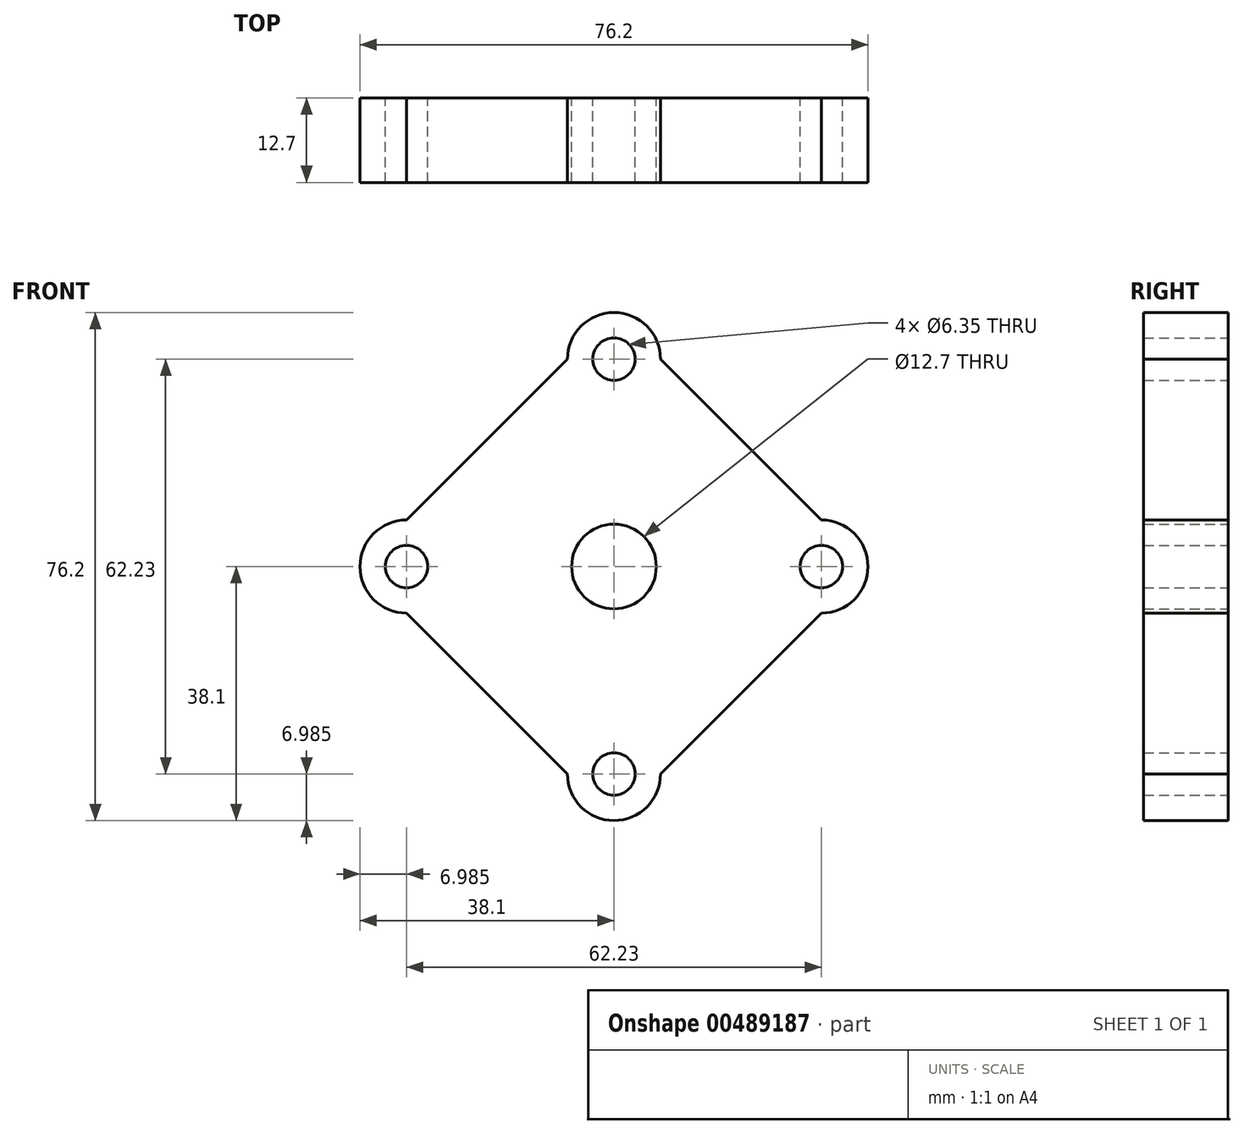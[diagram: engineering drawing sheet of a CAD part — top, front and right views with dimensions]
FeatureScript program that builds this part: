
annotation { "Feature Type Name" : "Feature", "Feature Type Description" : "" }
export const myFeature = defineFeature(function(context is Context, id is Id, definition is map)
    precondition{}
    {
        {
            var Q0;
            Q0=qCreatedBy(makeId("Front.planeOp"),FACE);
            var sketch = newSketch(context, id + "F0", { "sketchPlane" : qUnion([Q0])});
            skCircle(sketch, "E0", {"center": v(0, 0) * mm, "radius": 12.7 * mm});
            skCircle(sketch, "E1", {"center": v(0, 0) * mm, "radius": 6.35 * mm});
            skLineSegment(sketch, "E2", {"start": v(0, -12.7) * mm, "end": v(0, 38.1) * mm, "construction": true});
            skLineSegment(sketch, "E3", {"start": v(12.7, 0) * mm, "end": v(-38.1, 0) * mm, "construction": true});
            skLineSegment(sketch, "E4", {"start": v(0, 12.7) * mm, "end": v(0, -38.1) * mm, "construction": true});
            skPoint(sketch, "E4.endSnap0", {"position": v(0, 12.7) * mm});
            skLineSegment(sketch, "E5", {"start": v(-12.7, 0) * mm, "end": v(38.1, 0) * mm, "construction": true});
            skCircle(sketch, "E6", {"center": v(-31.12, 0) * mm, "radius": 6.99 * mm});
            skCircle(sketch, "E7", {"center": v(0, 31.11) * mm, "radius": 6.99 * mm});
            skCircle(sketch, "E8", {"center": v(0, -31.12) * mm, "radius": 6.99 * mm});
            skCircle(sketch, "E9", {"center": v(31.12, 0) * mm, "radius": 6.99 * mm});
            skPoint(sketch, "E10.0.midPoint", {"position": v(0, -38.1) * mm});
            skLineSegment(sketch, "E11", {"start": v(-31.12, 6.99) * mm, "end": v(-6.99, 31.11) * mm});
            skLineSegment(sketch, "E12", {"start": v(-31.12, -6.99) * mm, "end": v(-6.98, -31.12) * mm});
            skLineSegment(sketch, "E13", {"start": v(6.99, -31.12) * mm, "end": v(31.12, -6.99) * mm});
            skLineSegment(sketch, "E14", {"start": v(31.12, 6.98) * mm, "end": v(6.98, 31.11) * mm});
            skCircle(sketch, "E15", {"center": v(-31.12, 0) * mm, "radius": 3.18 * mm});
            skCircle(sketch, "E16", {"center": v(0, 31.11) * mm, "radius": 3.18 * mm});
            skCircle(sketch, "E17", {"center": v(0, -31.12) * mm, "radius": 3.18 * mm});
            skCircle(sketch, "E18", {"center": v(31.12, 0) * mm, "radius": 3.18 * mm});
            skSolve(sketch);
        }
        {
            var Q0;
            Q0 = qSketchRegion(id + "F0", true);
            var Q1;
            Q1=makeQuery(id+"F0.imprint","IMPRINT",FACE,{"disambiguationData":[TD([[makeQuery(id+"F0.imprint","IMPRINT",EDGE,{"derivedFrom":sQuery(id+"F0.wireOp",EDGE,"E0")}),1.0]])]});
            extrude(context, id + "F1", {"entities" : qUnion([Q0, Q1]), "depth" : 12.7 * mm, "offsetDistance" : 25.4 * mm});
        }
    });
